# Revit family: Bernhardt_Design-Seating-Tables-Elevation
name_source: partatom
category: Furniture
revit_build: Autodesk Revit 2016 (Build: 20150714_1515(x64)
units: mm (PartAtom-declared; Revit-internal decimal feet)

## family parameters
Always vertical = Yes
Cut with Voids When Loaded = No
OmniClass Number = 23.40.20.00
OmniClass Title = General Furniture and Specialties
Room Calculation Point = No
Shared = No
Work Plane-Based = No

## types (16) — shared parameters
Manufacturer = Bernhardt Design
Model = Elevation
URL = http://www.bernhardtdesign.com

## per-type parameters (varying)
| type | AsymmetricFins | Metal | SymmetricalFins | TableHalfLength | TableHalfWidth | TableLength | TableWidth | Wood |
| Elevation T-V10MZC | Yes | Aluminum - Bronze Powdercoat | No | 15 1/2" | 15 1/2" | 15 1/2" | 15 1/2" | Bernhardt - Oak default |
| Elevation T-V10MZ9 | Yes | Aluminum - Bronze Powdercoat | No | 15 1/2" | 15 1/2" | 15 1/2" | 15 1/2" | Bernhardt - Walnut default |
| Elevation T-V10MZF | Yes | Aluminum - Bronze Powdercoat | No | 15 1/2" | 15 1/2" | 15 1/2" | 15 1/2" | White Laminate |
| Elevation T-V10MZ8 | Yes | Aluminum - Bronze Powdercoat | No | 15 1/2" | 15 1/2" | 15 1/2" | 15 1/2" | Corian |
| Elevation T-V10M38 | Yes | Aluminum - Matte Black Powdercoat | No | 15 1/2" | 15 1/2" | 15 1/2" | 15 1/2" | Corian |
| Elevation T-V10M39 | Yes | Aluminum - Matte Black Powdercoat | No | 15 1/2" | 15 1/2" | 15 1/2" | 15 1/2" | Bernhardt - Walnut default |
| Elevation T-V10M3C | Yes | Aluminum - Matte Black Powdercoat | No | 15 1/2" | 15 1/2" | 15 1/2" | 15 1/2" | Bernhardt - Oak default |
| Elevation T-V10M3F | Yes | Aluminum - Matte Black Powdercoat | No | 15 1/2" | 15 1/2" | 15 1/2" | 15 1/2" | White Laminate |
| Elevation T-V60MZF | No | Aluminum - Bronze Powdercoat | Yes | 14" | 18" | 14" | 18" | White Laminate |
| Elevation T-V60MZC | No | Aluminum - Bronze Powdercoat | Yes | 14" | 18" | 14" | 18" | Bernhardt - Oak default |
| Elevation T-V60MZ9 | No | Aluminum - Bronze Powdercoat | Yes | 14" | 18" | 14" | 18" | Bernhardt - Walnut default |
| Elevation T-V60MZ8 | No | Aluminum - Bronze Powdercoat | Yes | 14" | 18" | 14" | 18" | Corian |
| Elevation T-V60M3F | No | Aluminum - Matte Black Powdercoat | Yes | 14" | 18" | 14" | 18" | White Laminate |
| Elevation T-V60M3C | No | Aluminum - Matte Black Powdercoat | Yes | 14" | 18" | 14" | 18" | Bernhardt - Oak default |
| Elevation T-V60M39 | No | Aluminum - Matte Black Powdercoat | Yes | 14" | 18" | 14" | 18" | Bernhardt - Walnut default |
| Elevation T-V60M38 | No | Aluminum - Matte Black Powdercoat | Yes | 14" | 18" | 14" | 18" | Corian |

note: column(s) folded — value = type name in every type: SKU

## geometry (parser evidence)
native form markers: Sweep x3
no freeform markers — native parametric forms only
